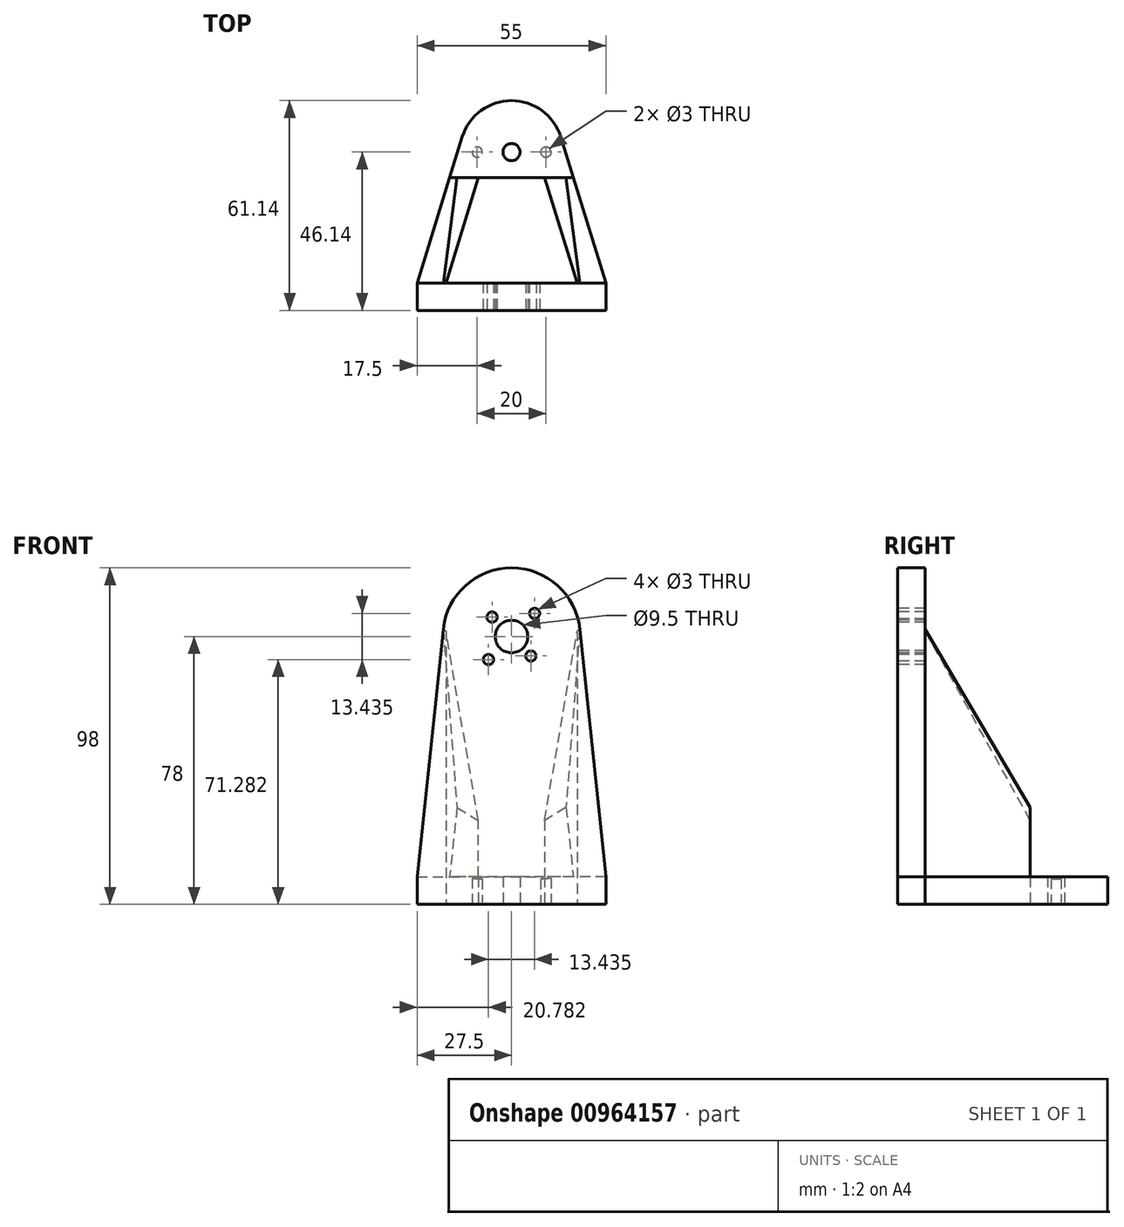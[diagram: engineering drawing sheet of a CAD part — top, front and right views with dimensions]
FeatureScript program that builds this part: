
annotation { "Feature Type Name" : "Feature", "Feature Type Description" : "" }
export const myFeature = defineFeature(function(context is Context, id is Id, definition is map)
    precondition{}
    {
        {
            var Q0;
            Q0=qCreatedBy(makeId("Top.planeOp"),FACE);
            var sketch = newSketch(context, id + "F0", { "sketchPlane" : qUnion([Q0])});
            skLineSegment(sketch, "E0.bottom", {"start": v(-27.5, 0) * mm, "end": v(27.5, 0) * mm});
            skLineSegment(sketch, "E0.top", {"start": v(-27.5, 8) * mm, "end": v(27.5, 8) * mm});
            skLineSegment(sketch, "E0.left", {"start": v(-27.5, 0) * mm, "end": v(-27.5, 8) * mm});
            skLineSegment(sketch, "E0.right", {"start": v(27.5, 0) * mm, "end": v(27.5, 8) * mm});
            skLineSegment(sketch, "E1", {"start": v(0, 8) * mm, "end": v(0, 46.14) * mm, "construction": true});
            skArc(sketch, "E2", {"start": v(14.33, 50.57) * mm, "mid": v(0, 61.14) * mm, "end": v(-14.33, 50.57) * mm});
            skLineSegment(sketch, "E3", {"start": v(-27.5, 8) * mm, "end": v(-16.47, 43.64) * mm});
            skLineSegment(sketch, "E4", {"start": v(27.5, 8) * mm, "end": v(16.47, 43.64) * mm});
            skCircle(sketch, "E5", {"center": v(0, 46.14) * mm, "radius": 2.5 * mm});
            skLineSegment(sketch, "E6", {"start": v(-10, 46.14) * mm, "end": v(10, 46.14) * mm, "construction": true});
            skCircle(sketch, "E7", {"center": v(-10, 46.14) * mm, "radius": 1.5 * mm});
            skCircle(sketch, "E8", {"center": v(10, 46.14) * mm, "radius": 1.5 * mm});
            skLineSegment(sketch, "E9", {"start": v(-16.47, 43.64) * mm, "end": v(-8.1, 43.64) * mm, "construction": true});
            skLineSegment(sketch, "E10", {"start": v(0, 43.64) * mm, "end": v(0, 38.64) * mm, "construction": true});
            skLineSegment(sketch, "E11", {"start": v(-16.47, 43.64) * mm, "end": v(-14.33, 50.57) * mm});
            skLineSegment(sketch, "E12", {"start": v(16.47, 43.64) * mm, "end": v(14.33, 50.57) * mm});
            skLineSegment(sketch, "E13", {"start": v(-19.13, 8) * mm, "end": v(-9.65, 38.64) * mm});
            skLineSegment(sketch, "E14", {"start": v(9.65, 38.64) * mm, "end": v(19.13, 8) * mm});
            skLineSegment(sketch, "E15", {"start": v(-9.65, 38.64) * mm, "end": v(9.65, 38.64) * mm});
            skLineSegment(sketch, "E16.trimOffspring", {"start": v(-8.1, 43.64) * mm, "end": v(16.47, 43.64) * mm, "construction": true});
            skSolve(sketch);
        }
        {
            var Q0;
            Q0=qSketchRegion(id+"F0",true);
            extrude(context, id + "F1", {"entities" : qUnion([Q0]), "depth" : 8 * mm, "offsetDistance" : 25 * mm});
        }
        {
            var Q0;
            Q0=makeQuery(id+"F1.opExtrude","SWEPT_FACE",FACE,{"disambiguationData":[OSD([sQuery(id+"F0.wireOp",EDGE,"E0.bottom")])]});
            var sketch = newSketch(context, id + "F2", { "sketchPlane" : qUnion([Q0])});
            skLineSegment(sketch, "E17", {"start": v(0, 0) * mm, "end": v(0, 78) * mm, "construction": true});
            skArc(sketch, "E18", {"start": v(19.89, 80.1) * mm, "mid": v(0, 98) * mm, "end": v(-19.89, 80.1) * mm});
            skLineSegment(sketch, "E19", {"start": v(-27.5, 8) * mm, "end": v(-19.89, 80.1) * mm});
            skLineSegment(sketch, "E20", {"start": v(27.5, 8) * mm, "end": v(19.89, 80.1) * mm});
            skSolve(sketch);
        }
        {
            var Q0;
            Q0=qSketchRegion(id+"F2",true);
            var Q1;
            Q1=makeQuery(id+"F2.imprint","IMPRINT",FACE,{"disambiguationData":[TD([[makeQuery(id+"F2.imprint","IMPRINT",EDGE,{"derivedFrom":sQuery(id+"F2.wireOp",EDGE,"E18")}),1.0]])]});
            var Q2;
            {var subQ0=sQuery(id+"F0.wireOp",EDGE,"E0.bottom");Q2=makeQuery(id+"F2.imprint","IMPRINT",FACE,{"disambiguationData":[TD([[makeQuery(id+"F2.imprint","IMPRINT",EDGE,{"derivedFrom":makeQuery(id+"F1.opExtrude","CAP_EDGE",EDGE,{"disambiguationData":[OSD([subQ0])],"isStart":true})}),1.0]])]});}
            extrude(context, id + "F3", {"entities" : qUnion([Q0, Q1, Q2]), "operationType" : NewBodyOperationType.ADD, "oppositeDirection" : true, "depth" : 8 * mm, "offsetDistance" : 25 * mm});
        }
        {
            var Q0;
            {var subQ0=sQuery(id+"F0.wireOp",EDGE,"E0.bottom");Q0=makeQuery(id+"F3.boolean.opBoolean","MERGE",FACE,{"derivedFrom":[makeQuery(id+"F1.opExtrude","SWEPT_FACE",FACE,{"disambiguationData":[OSD([subQ0])]}),makeQuery(id+"F3.opExtrude","CAP_FACE",FACE,{"disambiguationData":[OSD([subQ0,sQuery(id+"F0.wireOp",EDGE,"E0.left"),sQuery(id+"F0.wireOp",EDGE,"E0.right"),sQuery(id+"F2.wireOp",EDGE,"E18"),sQuery(id+"F2.wireOp",EDGE,"E19"),sQuery(id+"F2.wireOp",EDGE,"E20")])],"isStart":true})]});}
            var sketch = newSketch(context, id + "F4", { "sketchPlane" : qUnion([Q0])});
            skPoint(sketch, "E21.0", {"position": v(0, 78) * mm});
            skCircle(sketch, "E22", {"center": v(0, 78) * mm, "radius": 4.75 * mm});
            skLineSegment(sketch, "E23", {"start": v(-6.72, 71.28) * mm, "end": v(6.72, 84.72) * mm, "construction": true});
            skLineSegment(sketch, "E24", {"start": v(5.66, 72.34) * mm, "end": v(-5.66, 83.66) * mm, "construction": true});
            skLineSegment(sketch, "E25", {"start": v(-20.11, 78) * mm, "end": v(20.11, 78) * mm, "construction": true});
            skCircle(sketch, "E26", {"center": v(-5.66, 83.66) * mm, "radius": 1.5 * mm});
            skCircle(sketch, "E27", {"center": v(6.72, 84.72) * mm, "radius": 1.5 * mm});
            skCircle(sketch, "E28", {"center": v(5.66, 72.34) * mm, "radius": 1.5 * mm});
            skCircle(sketch, "E29", {"center": v(-6.72, 71.28) * mm, "radius": 1.5 * mm});
            skSolve(sketch);
        }
        {
            var Q0;
            Q0=qSketchRegion(id+"F4",true);
            var Q1;
            Q1=makeQuery(id+"F3.boolean.opBoolean","MERGE",FACE,{"derivedFrom":[makeQuery(id+"F1.opExtrude","SWEPT_FACE",FACE,{"disambiguationData":[OSD([sQuery(id+"F0.wireOp",EDGE,"E0.top")])]}),makeQuery(id+"F3.opExtrude","CAP_FACE",FACE,{"disambiguationData":[OSD([sQuery(id+"F0.wireOp",EDGE,"E0.bottom"),sQuery(id+"F0.wireOp",EDGE,"E0.left"),sQuery(id+"F0.wireOp",EDGE,"E0.right"),sQuery(id+"F2.wireOp",EDGE,"E18"),sQuery(id+"F2.wireOp",EDGE,"E19"),sQuery(id+"F2.wireOp",EDGE,"E20")])],"isStart":false})]});
            extrude(context, id + "F5", {"entities" : qUnion([Q0]), "operationType" : NewBodyOperationType.REMOVE, "endBound" : BoundingType.UP_TO_SURFACE, "oppositeDirection" : true, "depth" : 25 * mm, "endBoundEntityFace" : qUnion([Q1]), "offsetDistance" : 25 * mm});
        }
        {
            var Q0;
            Q0=makeQuery(id+"F1.opExtrude","CAP_VERTEX",VERTEX,{"disambiguationData":[OSD([sQuery(id+"F0.wireOp",EDGE,"E2"),sQuery(id+"F0.wireOp",EDGE,"E12")])],"isStart":false});
            var Q1;
            {var subQ0=sQuery(id+"F0.wireOp",EDGE,"E0.right");Q1=makeQuery(id+"F3.boolean.opBoolean","MERGE",VERTEX,{"derivedFrom":[makeQuery(id+"F1.opExtrude","CAP_VERTEX",VERTEX,{"disambiguationData":[OSD([sQuery(id+"F0.wireOp",EDGE,"E0.top"),subQ0,sQuery(id+"F0.wireOp",EDGE,"E4")])],"isStart":false}),makeQuery(id+"F3.opExtrude","CAP_VERTEX",VERTEX,{"disambiguationData":[OSD([sQuery(id+"F0.wireOp",EDGE,"E0.bottom"),subQ0,sQuery(id+"F2.wireOp",EDGE,"E20")])],"isStart":false})]});}
            var Q2;
            Q2=makeQuery(id+"F3.opExtrude","CAP_VERTEX",VERTEX,{"disambiguationData":[OSD([sQuery(id+"F2.wireOp",EDGE,"E18"),sQuery(id+"F2.wireOp",EDGE,"E20")])],"isStart":false});
            cPlane(context, id + "F6", {"entities" : qUnion([Q0, Q1, Q2]), "cplaneType" : CPlaneType.THREE_POINT, "offset" : 25 * mm, "width" : 150 * mm, "height" : 150 * mm});
        }
        {
            var Q0;
            Q0=qCreatedBy(id+"F6.planeOp",FACE);
            var sketch = newSketch(context, id + "F7", { "sketchPlane" : qUnion([Q0])});
            skLineSegment(sketch, "E30.0", {"start": v(-0.64, 5.07) * mm, "end": v(-0.64, 77.57) * mm});
            skLineSegment(sketch, "E31.0", {"start": v(-0.64, 5.07) * mm, "end": v(43.9, 6.45) * mm});
            skLineSegment(sketch, "E32", {"start": v(-0.64, 77.57) * mm, "end": v(43.9, 6.45) * mm});
            skSolve(sketch);
        }
        {
            var Q0;
            Q0=qSketchRegion(id+"F7",true);
            var Q1;
            Q1=makeQuery(id+"F1.opExtrude","SWEPT_FACE",FACE,{"disambiguationData":[OSD([sQuery(id+"F0.wireOp",EDGE,"E14")])]});
            extrude(context, id + "F8", {"entities" : qUnion([Q0]), "operationType" : NewBodyOperationType.ADD, "endBound" : BoundingType.UP_TO_SURFACE, "oppositeDirection" : true, "depth" : 25 * mm, "endBoundEntityFace" : qUnion([Q1]), "offsetDistance" : 25 * mm});
        }
        {
            var Q0;
            Q0=makeQuery(id+"F1.opExtrude","CAP_VERTEX",VERTEX,{"disambiguationData":[OSD([sQuery(id+"F0.wireOp",EDGE,"E2"),sQuery(id+"F0.wireOp",EDGE,"E11")])],"isStart":false});
            var Q1;
            {var subQ0=sQuery(id+"F0.wireOp",EDGE,"E0.left");Q1=makeQuery(id+"F3.boolean.opBoolean","MERGE",VERTEX,{"derivedFrom":[makeQuery(id+"F1.opExtrude","CAP_VERTEX",VERTEX,{"disambiguationData":[OSD([sQuery(id+"F0.wireOp",EDGE,"E0.top"),subQ0,sQuery(id+"F0.wireOp",EDGE,"E3")])],"isStart":false}),makeQuery(id+"F3.opExtrude","CAP_VERTEX",VERTEX,{"disambiguationData":[OSD([sQuery(id+"F0.wireOp",EDGE,"E0.bottom"),subQ0,sQuery(id+"F2.wireOp",EDGE,"E19")])],"isStart":false})]});}
            var Q2;
            Q2=makeQuery(id+"F3.opExtrude","CAP_VERTEX",VERTEX,{"disambiguationData":[OSD([sQuery(id+"F2.wireOp",EDGE,"E18"),sQuery(id+"F2.wireOp",EDGE,"E19")])],"isStart":false});
            cPlane(context, id + "F9", {"entities" : qUnion([Q0, Q1, Q2]), "cplaneType" : CPlaneType.THREE_POINT, "offset" : 25 * mm, "width" : 150 * mm, "height" : 150 * mm});
        }
        {
            var Q0;
            Q0=qCreatedBy(id+"F9.planeOp",FACE);
            var sketch = newSketch(context, id + "F10", { "sketchPlane" : qUnion([Q0])});
            skLineSegment(sketch, "E33.0", {"start": v(-0.64, 5.07) * mm, "end": v(-0.64, 77.57) * mm});
            skLineSegment(sketch, "E34.0", {"start": v(-0.64, 5.07) * mm, "end": v(43.9, 6.45) * mm});
            skLineSegment(sketch, "E35", {"start": v(-0.64, 77.57) * mm, "end": v(43.9, 6.45) * mm});
            skSolve(sketch);
        }
        {
            var Q0;
            Q0=qSketchRegion(id+"F10",true);
            var Q1;
            Q1=makeQuery(id+"F1.opExtrude","SWEPT_FACE",FACE,{"disambiguationData":[OSD([sQuery(id+"F0.wireOp",EDGE,"E13")])]});
            extrude(context, id + "F11", {"entities" : qUnion([Q0]), "operationType" : NewBodyOperationType.ADD, "endBound" : BoundingType.UP_TO_SURFACE, "depth" : 25 * mm, "endBoundEntityFace" : qUnion([Q1]), "offsetDistance" : 25 * mm});
        }
        {
            var Q0;
            Q0=makeQuery(id+"F1.opExtrude","CAP_FACE",FACE,{"disambiguationData":[OSD([sQuery(id+"F0.wireOp",EDGE,"E0.bottom"),sQuery(id+"F0.wireOp",EDGE,"E0.top"),sQuery(id+"F0.wireOp",EDGE,"E0.left"),sQuery(id+"F0.wireOp",EDGE,"E0.right"),sQuery(id+"F0.wireOp",EDGE,"E2"),sQuery(id+"F0.wireOp",EDGE,"E3"),sQuery(id+"F0.wireOp",EDGE,"E4"),sQuery(id+"F0.wireOp",EDGE,"E5"),sQuery(id+"F0.wireOp",EDGE,"E7"),sQuery(id+"F0.wireOp",EDGE,"E8"),sQuery(id+"F0.wireOp",EDGE,"E11"),sQuery(id+"F0.wireOp",EDGE,"E12"),sQuery(id+"F0.wireOp",EDGE,"E13"),sQuery(id+"F0.wireOp",EDGE,"E14"),sQuery(id+"F0.wireOp",EDGE,"E15")])],"isStart":false});
            var sketch = newSketch(context, id + "F12", { "sketchPlane" : qUnion([Q0])});
            skLineSegment(sketch, "E36.0.2", {"start": v(-9.65, 38.64) * mm, "end": v(9.65, 38.64) * mm});
            skArc(sketch, "E36.0.5", {"start": v(14.33, 50.57) * mm, "mid": v(0, 61.14) * mm, "end": v(-14.33, 50.57) * mm});
            skLineSegment(sketch, "E37.0", {"start": v(-18.02, 38.64) * mm, "end": v(-14.33, 50.57) * mm});
            skLineSegment(sketch, "E38.0", {"start": v(18.02, 38.64) * mm, "end": v(14.33, 50.57) * mm});
            skLineSegment(sketch, "E39", {"start": v(9.65, 38.64) * mm, "end": v(18.02, 38.64) * mm});
            skLineSegment(sketch, "E40", {"start": v(-9.65, 38.64) * mm, "end": v(-18.02, 38.64) * mm});
            skPoint(sketch, "E41.orphan", {"position": v(-27.5, 8) * mm});
            skPoint(sketch, "E42.orphan", {"position": v(27.5, 8) * mm});
            skPoint(sketch, "E36.0.3.end.orphan", {"position": v(6.83, 47.76) * mm});
            skPoint(sketch, "E36.0.0.end.orphan", {"position": v(-6.83, 47.76) * mm});
            skSolve(sketch);
        }
        {
            var Q0;
            Q0=qSketchRegion(id+"F12",true);
            extrude(context, id + "F13", {"entities" : qUnion([Q0]), "operationType" : NewBodyOperationType.REMOVE, "depth" : 25 * mm, "offsetDistance" : 25 * mm});
        }
    });
